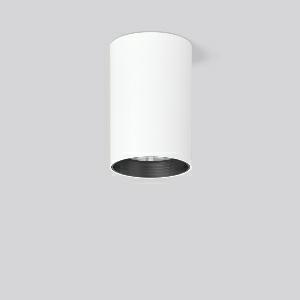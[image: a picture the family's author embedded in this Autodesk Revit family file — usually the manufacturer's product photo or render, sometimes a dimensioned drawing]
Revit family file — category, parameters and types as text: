
# Revit family: heledon_maxi_a_931229_002_2_76_9fef
name_source: partatom
category: Lighting Fixtures
units: mm (PartAtom-declared; Revit-internal decimal feet)

## family parameters
Cut with Voids When Loaded = No
Host = Face
Light Source = No
Part Type = Normal
Room Calculation Point = No
Round Connector Dimension = Use Diameter
Shared = No

## types (1)
- HELEDON maxi A (1 x LED Modul 927, 3450 lm, 2700)
    Apparent Load = 35 VA
    Approval mark = CE
    CIE Flux Codes = 96 100 100 100 100
    Color Rendering = 92
    Color Temperature = 2700
    Default Elevation = 1800 mm
    Description = Series: HELEDON maxi
Cylindrical surface-mounted downlight. Housing: die-cast aluminium, powder-coated. Internal ceiling frame polycarbonate with bayonet mounting. Black plastic ring and recessed LED to prevent glare from the side. Optical assembly with lens made of plastic (polycarbonate) for the best homogeneous light distribution - can be changed without tools. Best colour rendering index Ra>90. Suitable for Ceiling mounting. Easy installation with a separate ceiling frame with bayonet mounting and plug connection. Driver integrated. Connected via plug-in connector. High quality converter without flickering and stroboscopic effect. The following accessories can be mounted without use of tools: interchangeable lenses, decorative glasses, honeycomb louvre, clear and frosted diffusers, white interchangeable plastic ring. 
Colour: traffic white, matt (RAL 9016)
Diameter: 123 mm
Height: 183 mm
Lamp: LED
Socket: without socket
Colour temperature: 2700K
Colour rendering index (CRI): 92
System power: 35 W
Rated luminous flux: 3450 lm
Luminous efficiency: 99 lm/W
Control gear: Converter, dimmable, DALI
Protection class: I
Type of protection: IP 20
    Height = 183 mm
    Lamp = 1 x LED Modul 927
    Lamp Light Flux = 3450 lm
    Lamp count = 1
    Length = 123 mm
    Lifetime = 50000 h
    Luminous efficacy = 99 lm/W
    Manufacturer = RZB
    ModVariant = No
    Model = 931229.002.2.76
    Mounting Place = Ceiling
    Mounting Type = Surface mounted
    Number of Poles = 1
    OnlyDefault = Yes
    Power Factor = 1
    Product Name = HELEDON maxi A
    Product group = Surface mounted downlights
    ProductGroupID = 302
    Protection Class = Protection class I
    Protection Degree = IP 20
    RLX_Detail_Level = 1
    RLX_Emergency_Light_Flux = 0 lm
    RLX_Emergency_Type = 0
    RLX_Emergency_Type_DB = No
    RlxData = <blob elided: 96953 chars, md5=ee03e7d6>
    Socket = socket
    Standby Power = 0 W
    System Light Flux = 3450 lm
    System Power = 35 W
    Type Comments = Product without accessories
    Type Image = 931193.002.jpg
    URL = http://relux.com
    VarID = ---
    Voltage = 230 V
    Voltage Range = 220-240 V
    Weight = 0.00 kg
    Width = 0 mm  [stored 0 ft]

note: [stored X ft] marks values corroborated as IEEE doubles in the binary element streams (Revit-internal decimal feet)

## geometry (parser evidence)
native form markers: Blend x4, Sweep x11
no freeform markers — native parametric forms only
